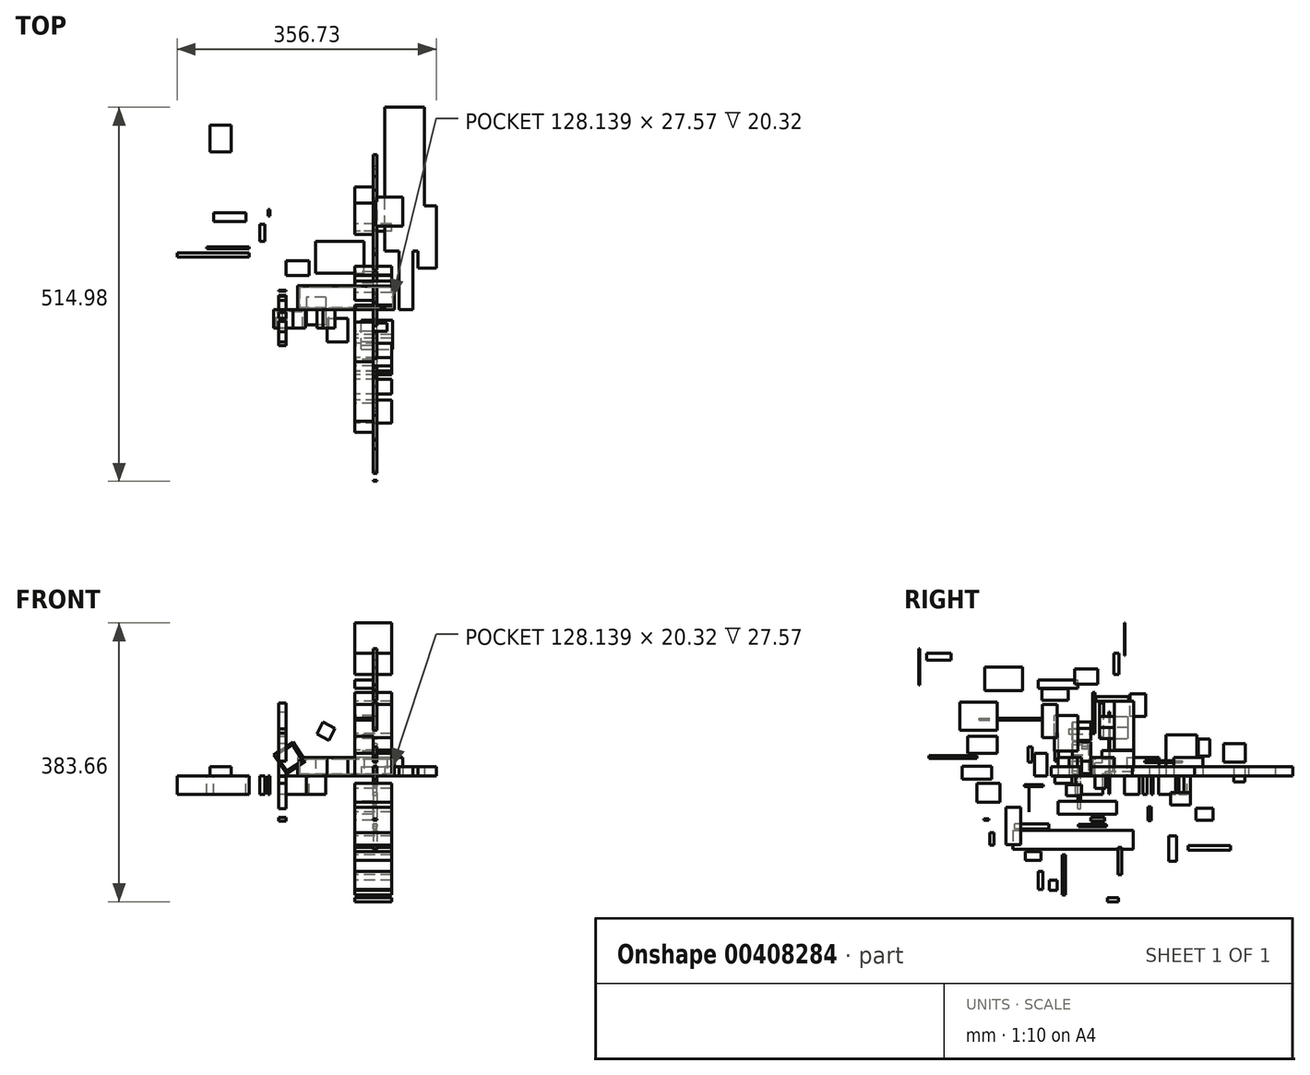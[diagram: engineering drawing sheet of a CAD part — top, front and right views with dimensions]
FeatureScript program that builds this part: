
annotation { "Feature Type Name" : "Feature", "Feature Type Description" : "" }
export const myFeature = defineFeature(function(context is Context, id is Id, definition is map)
    precondition{}
    {
        {
            var Q0;
            Q0=qCreatedBy(makeId("Top.planeOp"),FACE);
            var sketch = newSketch(context, id + "F0", { "sketchPlane" : qUnion([Q0])});
            skLineSegment(sketch, "E0.bottom", {"start": v(-38.03, -44.82) * mm, "end": v(-9.47, -44.82) * mm});
            skLineSegment(sketch, "E0.top", {"start": v(-38.03, -12.4) * mm, "end": v(-9.47, -12.4) * mm});
            skLineSegment(sketch, "E0.left", {"start": v(-38.03, -44.82) * mm, "end": v(-38.03, -12.4) * mm});
            skLineSegment(sketch, "E0.right", {"start": v(-9.47, -44.82) * mm, "end": v(-9.47, -12.4) * mm});
            skLineSegment(sketch, "E1.bottom", {"start": v(44.25, -18.44) * mm, "end": v(0, -18.44) * mm});
            skLineSegment(sketch, "E1.top", {"start": v(44.25, -29.9) * mm, "end": v(0, -29.9) * mm});
            skLineSegment(sketch, "E1.left", {"start": v(44.25, -18.44) * mm, "end": v(44.25, -29.9) * mm});
            skLineSegment(sketch, "E1.right", {"start": v(0, -18.44) * mm, "end": v(0, -29.9) * mm});
            skLineSegment(sketch, "E2.bottom", {"start": v(54.75, 32.65) * mm, "end": v(-78.47, 32.65) * mm});
            skLineSegment(sketch, "E2.top", {"start": v(54.75, 0) * mm, "end": v(-78.47, 0) * mm});
            skLineSegment(sketch, "E2.left", {"start": v(54.75, 32.65) * mm, "end": v(54.75, 0) * mm});
            skLineSegment(sketch, "E2.right", {"start": v(-78.47, 32.65) * mm, "end": v(-78.47, 0) * mm});
            skLineSegment(sketch, "E3.bottom", {"start": v(-53.9, 49.58) * mm, "end": v(12.77, 49.58) * mm});
            skLineSegment(sketch, "E3.top", {"start": v(-53.9, 93.96) * mm, "end": v(12.77, 93.96) * mm});
            skLineSegment(sketch, "E3.left", {"start": v(-53.9, 49.58) * mm, "end": v(-53.9, 93.96) * mm});
            skLineSegment(sketch, "E3.right", {"start": v(12.77, 49.58) * mm, "end": v(12.77, 93.96) * mm});
            skLineSegment(sketch, "E4.bottom", {"start": v(28.6, 114.54) * mm, "end": v(66.24, 114.54) * mm});
            skLineSegment(sketch, "E4.top", {"start": v(28.6, 154.62) * mm, "end": v(66.24, 154.62) * mm});
            skLineSegment(sketch, "E4.left", {"start": v(28.6, 114.54) * mm, "end": v(28.6, 154.62) * mm});
            skLineSegment(sketch, "E4.right", {"start": v(66.24, 114.54) * mm, "end": v(66.24, 154.62) * mm});
            skSolve(sketch);
        }
        {
            var Q0;
            Q0 = qSketchRegion(id + "F0", true);
            extrude(context, id + "F1", {"entities" : qUnion([Q0]), "depth" : 25.4 * mm});
        }
        {
            var Q0;
            Q0=qCreatedBy(makeId("Right.planeOp"),FACE);
            var sketch = newSketch(context, id + "F2", { "sketchPlane" : qUnion([Q0])});
            skLineSegment(sketch, "E5.bottom", {"start": v(-45, -52.84) * mm, "end": v(35.7, -52.84) * mm});
            skLineSegment(sketch, "E5.top", {"start": v(-45, -35) * mm, "end": v(35.7, -35) * mm});
            skLineSegment(sketch, "E5.left", {"start": v(-45, -52.84) * mm, "end": v(-45, -35) * mm});
            skLineSegment(sketch, "E5.right", {"start": v(35.7, -52.84) * mm, "end": v(35.7, -35) * mm});
            skLineSegment(sketch, "E6.bottom", {"start": v(-18, 34.28) * mm, "end": v(-49.8, 34.28) * mm});
            skLineSegment(sketch, "E6.top", {"start": v(-18, 83.43) * mm, "end": v(-49.8, 83.43) * mm});
            skLineSegment(sketch, "E6.left", {"start": v(-18, 34.28) * mm, "end": v(-18, 83.43) * mm});
            skLineSegment(sketch, "E6.right", {"start": v(-49.8, 34.28) * mm, "end": v(-49.8, 83.43) * mm});
            skLineSegment(sketch, "E7.bottom", {"start": v(12.3, 51.35) * mm, "end": v(51.6, 51.35) * mm});
            skLineSegment(sketch, "E7.top", {"start": v(12.3, 82.1) * mm, "end": v(51.6, 82.1) * mm});
            skLineSegment(sketch, "E7.left", {"start": v(12.3, 51.35) * mm, "end": v(12.3, 82.1) * mm});
            skLineSegment(sketch, "E7.right", {"start": v(51.6, 51.35) * mm, "end": v(51.6, 82.1) * mm});
            skLineSegment(sketch, "E8.bottom", {"start": v(103.49, 56.5) * mm, "end": v(146.08, 56.5) * mm});
            skLineSegment(sketch, "E8.top", {"start": v(103.49, 0) * mm, "end": v(146.08, 0) * mm});
            skLineSegment(sketch, "E8.left", {"start": v(103.49, 56.5) * mm, "end": v(103.49, 0) * mm});
            skLineSegment(sketch, "E8.right", {"start": v(146.08, 56.5) * mm, "end": v(146.08, 0) * mm});
            skLineSegment(sketch, "E9.bottom", {"start": v(-169.48, 54.43) * mm, "end": v(-128.98, 54.43) * mm});
            skLineSegment(sketch, "E9.top", {"start": v(-169.48, 31.07) * mm, "end": v(-128.98, 31.07) * mm});
            skLineSegment(sketch, "E9.left", {"start": v(-169.48, 54.43) * mm, "end": v(-169.48, 31.07) * mm});
            skLineSegment(sketch, "E9.right", {"start": v(-128.98, 54.43) * mm, "end": v(-128.98, 31.07) * mm});
            skLineSegment(sketch, "E10.bottom", {"start": v(-153.88, 77.11) * mm, "end": v(-68.7, 77.11) * mm});
            skLineSegment(sketch, "E10.top", {"start": v(-153.88, 79.37) * mm, "end": v(-68.7, 79.37) * mm});
            skLineSegment(sketch, "E10.left", {"start": v(-153.88, 77.11) * mm, "end": v(-153.88, 79.37) * mm});
            skLineSegment(sketch, "E10.right", {"start": v(-68.7, 77.11) * mm, "end": v(-68.7, 79.37) * mm});
            skLineSegment(sketch, "E11.bottom", {"start": v(-72.3, 120.66) * mm, "end": v(-17.7, 120.66) * mm});
            skLineSegment(sketch, "E11.top", {"start": v(-72.3, 131.98) * mm, "end": v(-17.7, 131.98) * mm});
            skLineSegment(sketch, "E11.left", {"start": v(-72.3, 120.66) * mm, "end": v(-72.3, 131.98) * mm});
            skLineSegment(sketch, "E11.right", {"start": v(-17.7, 120.66) * mm, "end": v(-17.7, 131.98) * mm});
            skLineSegment(sketch, "E12.bottom", {"start": v(144.88, -60.84) * mm, "end": v(168.58, -60.84) * mm});
            skLineSegment(sketch, "E12.top", {"start": v(144.88, -44.28) * mm, "end": v(168.58, -44.28) * mm});
            skLineSegment(sketch, "E12.left", {"start": v(144.88, -60.84) * mm, "end": v(144.88, -44.28) * mm});
            skLineSegment(sketch, "E12.right", {"start": v(168.58, -60.84) * mm, "end": v(168.58, -44.28) * mm});
            skSolve(sketch);
        }
        {
            var Q0;
            Q0 = qSketchRegion(id + "F2", true);
            extrude(context, id + "F3", {"entities" : qUnion([Q0]), "depth" : 25.4 * mm});
        }
        {
            var Q0;
            Q0=qCreatedBy(makeId("Front.planeOp"),FACE);
            var sketch = newSketch(context, id + "F4", { "sketchPlane" : qUnion([Q0])});
            skCircle(sketch, "E13.cCircle", {"center": v(-89.7, 25.02) * mm, "radius": 22.2 * mm, "construction": true});
            skLineSegment(sketch, "E13.0", {"start": v(-85.2, 46.75) * mm, "end": v(-67.97, 20.52) * mm});
            skLineSegment(sketch, "E13.1", {"start": v(-67.97, 20.52) * mm, "end": v(-94.21, 3.28) * mm});
            skLineSegment(sketch, "E13.2", {"start": v(-94.21, 3.28) * mm, "end": v(-111.44, 29.52) * mm});
            skLineSegment(sketch, "E13.3", {"start": v(-111.44, 29.52) * mm, "end": v(-85.2, 46.75) * mm});
            skCircle(sketch, "E14.cCircle", {"center": v(-39.66, 61.63) * mm, "radius": 13.15 * mm, "construction": true});
            skLineSegment(sketch, "E14.0", {"start": v(-43.47, 74.22) * mm, "end": v(-27.08, 65.44) * mm});
            skLineSegment(sketch, "E14.1", {"start": v(-27.08, 65.44) * mm, "end": v(-35.85, 49.05) * mm});
            skLineSegment(sketch, "E14.2", {"start": v(-35.85, 49.05) * mm, "end": v(-52.24, 57.82) * mm});
            skLineSegment(sketch, "E14.3", {"start": v(-52.24, 57.82) * mm, "end": v(-43.47, 74.22) * mm});
            skSolve(sketch);
        }
        {
            var Q0;
            Q0=makeQuery(id+"F4.imprint","IMPRINT",FACE,{"disambiguationData":[TD([[makeQuery(id+"F4.imprint","IMPRINT",EDGE,{"derivedFrom":sQuery(id+"F4.wireOp",EDGE,"E13.0")}),-1.0]])]});
            var Q1;
            Q1=makeQuery(id+"F4.imprint","IMPRINT",FACE,{"disambiguationData":[TD([[makeQuery(id+"F4.imprint","IMPRINT",EDGE,{"derivedFrom":sQuery(id+"F4.wireOp",EDGE,"E14.0")}),-1.0]])]});
            extrude(context, id + "F5", {"entities" : qUnion([Q0, Q1]), "operationType" : NewBodyOperationType.ADD, "depth" : 25.4 * mm});
        }
        {
            var Q0;
            Q0=makeQuery(id+"F5.opExtrude","CAP_FACE",FACE,{"disambiguationData":[OSD([sQuery(id+"F4.wireOp",EDGE,"E13.0"),sQuery(id+"F4.wireOp",EDGE,"E13.1"),sQuery(id+"F4.wireOp",EDGE,"E13.2"),sQuery(id+"F4.wireOp",EDGE,"E13.3")])],"isStart":false});
            shell(context, id + "F6", {"entities" : qUnion([Q0]), "thickness" : 2.54 * mm});
        }
        {
            var Q0;
            Q0=qCreatedBy(makeId("Top.planeOp"),FACE);
            var sketch = newSketch(context, id + "F7", { "sketchPlane" : qUnion([Q0])});
            skLineSegment(sketch, "E15.bottom", {"start": v(8.87, -54.8) * mm, "end": v(52.17, -54.8) * mm});
            skLineSegment(sketch, "E15.top", {"start": v(8.87, -14.7) * mm, "end": v(52.17, -14.7) * mm});
            skLineSegment(sketch, "E15.left", {"start": v(8.87, -54.8) * mm, "end": v(8.87, -14.7) * mm});
            skLineSegment(sketch, "E15.right", {"start": v(52.17, -54.8) * mm, "end": v(52.17, -14.7) * mm});
            skLineSegment(sketch, "E16.bottom", {"start": v(61.23, 0) * mm, "end": v(79.8, 0) * mm});
            skLineSegment(sketch, "E16.top", {"start": v(61.23, 87.38) * mm, "end": v(79.8, 87.38) * mm});
            skLineSegment(sketch, "E16.left", {"start": v(61.23, 0) * mm, "end": v(61.23, 87.38) * mm});
            skLineSegment(sketch, "E16.right", {"start": v(79.8, 0) * mm, "end": v(79.8, 87.38) * mm});
            skLineSegment(sketch, "E17.bottom", {"start": v(-170.1, 253.84) * mm, "end": v(-199.66, 253.84) * mm});
            skLineSegment(sketch, "E17.top", {"start": v(-170.1, 217.1) * mm, "end": v(-199.66, 217.1) * mm});
            skLineSegment(sketch, "E17.left", {"start": v(-170.1, 253.84) * mm, "end": v(-170.1, 217.1) * mm});
            skLineSegment(sketch, "E17.right", {"start": v(-199.66, 253.84) * mm, "end": v(-199.66, 217.1) * mm});
            skLineSegment(sketch, "E18.bottom", {"start": v(96.2, 80.64) * mm, "end": v(41.3, 80.64) * mm});
            skLineSegment(sketch, "E18.top", {"start": v(96.2, 278.22) * mm, "end": v(41.3, 278.22) * mm});
            skLineSegment(sketch, "E18.left", {"start": v(96.2, 80.64) * mm, "end": v(96.2, 278.22) * mm});
            skLineSegment(sketch, "E18.right", {"start": v(41.3, 80.64) * mm, "end": v(41.3, 278.22) * mm});
            skLineSegment(sketch, "E19.bottom", {"start": v(112.24, 57.15) * mm, "end": v(87.1, 57.15) * mm});
            skLineSegment(sketch, "E19.top", {"start": v(112.24, 142.89) * mm, "end": v(87.1, 142.89) * mm});
            skLineSegment(sketch, "E19.left", {"start": v(112.24, 57.15) * mm, "end": v(112.24, 142.89) * mm});
            skLineSegment(sketch, "E19.right", {"start": v(87.1, 57.15) * mm, "end": v(87.1, 142.89) * mm});
            skSolve(sketch);
        }
        {
            var Q0;
            Q0 = qSketchRegion(id + "F7", true);
            extrude(context, id + "F8", {"entities" : qUnion([Q0]), "depth" : 12.7 * mm});
        }
        {
            var Q0;
            Q0=makeQuery(id+"F3.opExtrude","CAP_FACE",FACE,{"disambiguationData":[OSD([sQuery(id+"F2.wireOp",EDGE,"E7.bottom"),sQuery(id+"F2.wireOp",EDGE,"E7.top"),sQuery(id+"F2.wireOp",EDGE,"E7.left"),sQuery(id+"F2.wireOp",EDGE,"E7.right")])],"isStart":false});
            var sketch = newSketch(context, id + "F9", { "sketchPlane" : qUnion([Q0])});
            skLineSegment(sketch, "E20.bottom", {"start": v(-22.37, 126.65) * mm, "end": v(9.5, 126.65) * mm});
            skLineSegment(sketch, "E20.top", {"start": v(-22.37, 147.22) * mm, "end": v(9.5, 147.22) * mm});
            skLineSegment(sketch, "E20.left", {"start": v(-22.37, 126.65) * mm, "end": v(-22.37, 147.22) * mm});
            skLineSegment(sketch, "E20.right", {"start": v(9.5, 126.65) * mm, "end": v(9.5, 147.22) * mm});
            skPoint(sketch, "E21.firstSnap0", {"position": v(12.3, 66.72) * mm});
            skPoint(sketch, "E21.oppositeSnap0", {"position": v(12.3, 66.72) * mm});
            skLineSegment(sketch, "E21.bottom", {"start": v(39.3, 66.72) * mm, "end": v(63.45, 66.72) * mm});
            skLineSegment(sketch, "E21.top", {"start": v(39.3, 66.72) * mm, "end": v(63.45, 66.72) * mm});
            skLineSegment(sketch, "E21.left", {"start": v(39.3, 66.72) * mm, "end": v(39.3, 66.72) * mm});
            skLineSegment(sketch, "E21.right", {"start": v(63.45, 66.72) * mm, "end": v(63.45, 66.72) * mm});
            skLineSegment(sketch, "E22.bottom", {"start": v(51.38, 66.72) * mm, "end": v(12.3, 66.72) * mm});
            skLineSegment(sketch, "E22.top", {"start": v(51.38, 82.1) * mm, "end": v(12.3, 82.1) * mm});
            skLineSegment(sketch, "E22.left", {"start": v(51.38, 66.72) * mm, "end": v(51.38, 82.1) * mm});
            skLineSegment(sketch, "E22.right", {"start": v(12.3, 66.72) * mm, "end": v(12.3, 82.1) * mm});
            skLineSegment(sketch, "E23.bottom", {"start": v(75.5, 81.79) * mm, "end": v(54.2, 81.79) * mm});
            skLineSegment(sketch, "E23.top", {"start": v(75.5, 113.11) * mm, "end": v(54.2, 113.11) * mm});
            skLineSegment(sketch, "E23.left", {"start": v(75.5, 81.79) * mm, "end": v(75.5, 113.11) * mm});
            skLineSegment(sketch, "E23.right", {"start": v(54.2, 81.79) * mm, "end": v(54.2, 113.11) * mm});
            skLineSegment(sketch, "E24.bottom", {"start": v(52.46, 109.2) * mm, "end": v(6.87, 109.2) * mm});
            skLineSegment(sketch, "E24.top", {"start": v(52.46, 103.02) * mm, "end": v(6.87, 103.02) * mm});
            skLineSegment(sketch, "E24.left", {"start": v(52.46, 109.2) * mm, "end": v(52.46, 103.02) * mm});
            skLineSegment(sketch, "E24.right", {"start": v(6.87, 109.2) * mm, "end": v(6.87, 103.02) * mm});
            skLineSegment(sketch, "E25.bottom", {"start": v(-31, 104.25) * mm, "end": v(-67.36, 104.25) * mm});
            skLineSegment(sketch, "E25.top", {"start": v(-31, 120.08) * mm, "end": v(-67.36, 120.08) * mm});
            skLineSegment(sketch, "E25.left", {"start": v(-31, 104.25) * mm, "end": v(-31, 120.08) * mm});
            skLineSegment(sketch, "E25.right", {"start": v(-67.36, 104.25) * mm, "end": v(-67.36, 120.08) * mm});
            skLineSegment(sketch, "E26.bottom", {"start": v(-93.6, 117.55) * mm, "end": v(-145.86, 117.55) * mm});
            skLineSegment(sketch, "E26.top", {"start": v(-93.6, 149.62) * mm, "end": v(-145.86, 149.62) * mm});
            skLineSegment(sketch, "E26.left", {"start": v(-93.6, 117.55) * mm, "end": v(-93.6, 149.62) * mm});
            skLineSegment(sketch, "E26.right", {"start": v(-145.86, 117.55) * mm, "end": v(-145.86, 149.62) * mm});
            skLineSegment(sketch, "E27.bottom", {"start": v(-192.33, 159.6) * mm, "end": v(-225.98, 159.6) * mm});
            skLineSegment(sketch, "E27.top", {"start": v(-192.33, 169.05) * mm, "end": v(-225.98, 169.05) * mm});
            skLineSegment(sketch, "E27.left", {"start": v(-192.33, 159.6) * mm, "end": v(-192.33, 169.05) * mm});
            skLineSegment(sketch, "E27.right", {"start": v(-225.98, 159.6) * mm, "end": v(-225.98, 169.05) * mm});
            skLineSegment(sketch, "E28.bottom", {"start": v(-236.76, 175.63) * mm, "end": v(-235.24, 175.63) * mm});
            skLineSegment(sketch, "E28.top", {"start": v(-236.76, 125.14) * mm, "end": v(-235.24, 125.14) * mm});
            skLineSegment(sketch, "E28.left", {"start": v(-236.76, 175.63) * mm, "end": v(-236.76, 125.14) * mm});
            skLineSegment(sketch, "E28.right", {"start": v(-235.24, 175.63) * mm, "end": v(-235.24, 125.14) * mm});
            skLineSegment(sketch, "E29.bottom", {"start": v(-180.07, 101.93) * mm, "end": v(-128.76, 101.93) * mm});
            skLineSegment(sketch, "E29.top", {"start": v(-180.07, 62.9) * mm, "end": v(-128.76, 62.9) * mm});
            skLineSegment(sketch, "E29.left", {"start": v(-180.07, 101.93) * mm, "end": v(-180.07, 62.9) * mm});
            skLineSegment(sketch, "E29.right", {"start": v(-128.76, 101.93) * mm, "end": v(-128.76, 62.9) * mm});
            skLineSegment(sketch, "E30.bottom", {"start": v(-86.12, 40.02) * mm, "end": v(-80.28, 40.02) * mm});
            skLineSegment(sketch, "E30.top", {"start": v(-86.12, 19.17) * mm, "end": v(-80.28, 19.17) * mm});
            skLineSegment(sketch, "E30.left", {"start": v(-86.12, 40.02) * mm, "end": v(-86.12, 19.17) * mm});
            skLineSegment(sketch, "E30.right", {"start": v(-80.28, 40.02) * mm, "end": v(-80.28, 19.17) * mm});
            skLineSegment(sketch, "E31.bottom", {"start": v(-156.85, 24.07) * mm, "end": v(-222.57, 24.07) * mm});
            skLineSegment(sketch, "E31.top", {"start": v(-156.85, 28.24) * mm, "end": v(-222.57, 28.24) * mm});
            skLineSegment(sketch, "E31.left", {"start": v(-156.85, 24.07) * mm, "end": v(-156.85, 28.24) * mm});
            skLineSegment(sketch, "E31.right", {"start": v(-222.57, 24.07) * mm, "end": v(-222.57, 28.24) * mm});
            skLineSegment(sketch, "E32.bottom", {"start": v(-177.26, 13.33) * mm, "end": v(-136.14, 13.33) * mm});
            skLineSegment(sketch, "E32.top", {"start": v(-177.26, -4.55) * mm, "end": v(-136.14, -4.55) * mm});
            skLineSegment(sketch, "E32.left", {"start": v(-177.26, 13.33) * mm, "end": v(-177.26, -4.55) * mm});
            skLineSegment(sketch, "E32.right", {"start": v(-136.14, 13.33) * mm, "end": v(-136.14, -4.55) * mm});
            skLineSegment(sketch, "E33.bottom", {"start": v(-91.53, -12.28) * mm, "end": v(-65.22, -12.28) * mm});
            skLineSegment(sketch, "E33.top", {"start": v(-91.53, -14.84) * mm, "end": v(-65.22, -14.84) * mm});
            skLineSegment(sketch, "E33.left", {"start": v(-91.53, -12.28) * mm, "end": v(-91.53, -14.84) * mm});
            skLineSegment(sketch, "E33.right", {"start": v(-65.22, -12.28) * mm, "end": v(-65.22, -14.84) * mm});
            skLineSegment(sketch, "E34.bottom", {"start": v(-33.36, -27.12) * mm, "end": v(-12.85, -27.12) * mm});
            skLineSegment(sketch, "E34.top", {"start": v(-33.36, -12.23) * mm, "end": v(-12.85, -12.23) * mm});
            skLineSegment(sketch, "E34.left", {"start": v(-33.36, -27.12) * mm, "end": v(-33.36, -12.23) * mm});
            skLineSegment(sketch, "E34.right", {"start": v(-12.85, -27.12) * mm, "end": v(-12.85, -12.23) * mm});
            skLineSegment(sketch, "E35.bottom", {"start": v(20.29, -17.13) * mm, "end": v(5.9, -17.13) * mm});
            skLineSegment(sketch, "E35.top", {"start": v(20.29, 17.72) * mm, "end": v(5.9, 17.72) * mm});
            skLineSegment(sketch, "E35.left", {"start": v(20.29, -17.13) * mm, "end": v(20.29, 17.72) * mm});
            skLineSegment(sketch, "E35.right", {"start": v(5.9, -17.13) * mm, "end": v(5.9, 17.72) * mm});
            skLineSegment(sketch, "E36.bottom", {"start": v(15.53, 35.04) * mm, "end": v(59.45, 35.04) * mm});
            skLineSegment(sketch, "E36.top", {"start": v(15.53, 6.29) * mm, "end": v(59.45, 6.29) * mm});
            skLineSegment(sketch, "E36.left", {"start": v(15.53, 35.04) * mm, "end": v(15.53, 6.29) * mm});
            skLineSegment(sketch, "E36.right", {"start": v(59.45, 35.04) * mm, "end": v(59.45, 6.29) * mm});
            skLineSegment(sketch, "E37.bottom", {"start": v(74.66, 20.84) * mm, "end": v(126.05, 20.84) * mm});
            skLineSegment(sketch, "E37.top", {"start": v(74.66, 18.19) * mm, "end": v(126.05, 18.19) * mm});
            skLineSegment(sketch, "E37.left", {"start": v(74.66, 20.84) * mm, "end": v(74.66, 18.19) * mm});
            skLineSegment(sketch, "E37.right", {"start": v(126.05, 20.84) * mm, "end": v(126.05, 18.19) * mm});
            skLineSegment(sketch, "E38.bottom", {"start": v(164.01, 27.43) * mm, "end": v(148.04, 27.43) * mm});
            skLineSegment(sketch, "E38.top", {"start": v(164.01, 51.07) * mm, "end": v(148.04, 51.07) * mm});
            skLineSegment(sketch, "E38.left", {"start": v(164.01, 27.43) * mm, "end": v(164.01, 51.07) * mm});
            skLineSegment(sketch, "E38.right", {"start": v(148.04, 27.43) * mm, "end": v(148.04, 51.07) * mm});
            skLineSegment(sketch, "E39.bottom", {"start": v(182.96, 44.39) * mm, "end": v(212.85, 44.39) * mm});
            skLineSegment(sketch, "E39.top", {"start": v(182.96, 19.27) * mm, "end": v(212.85, 19.27) * mm});
            skLineSegment(sketch, "E39.left", {"start": v(182.96, 44.39) * mm, "end": v(182.96, 19.27) * mm});
            skLineSegment(sketch, "E39.right", {"start": v(212.85, 44.39) * mm, "end": v(212.85, 19.27) * mm});
            skLineSegment(sketch, "E40.bottom", {"start": v(212.17, 11.5) * mm, "end": v(197.14, 11.5) * mm});
            skLineSegment(sketch, "E40.top", {"start": v(212.17, -8) * mm, "end": v(197.14, -8) * mm});
            skLineSegment(sketch, "E40.left", {"start": v(212.17, 11.5) * mm, "end": v(212.17, -8) * mm});
            skLineSegment(sketch, "E40.right", {"start": v(197.14, 11.5) * mm, "end": v(197.14, -8) * mm});
            skLineSegment(sketch, "E41.bottom", {"start": v(137.05, -22.66) * mm, "end": v(110.1, -22.66) * mm});
            skLineSegment(sketch, "E41.top", {"start": v(137.05, -39.9) * mm, "end": v(110.1, -39.9) * mm});
            skLineSegment(sketch, "E41.left", {"start": v(137.05, -22.66) * mm, "end": v(137.05, -39.9) * mm});
            skLineSegment(sketch, "E41.right", {"start": v(110.1, -22.66) * mm, "end": v(110.1, -39.9) * mm});
            skLineSegment(sketch, "E42.bottom", {"start": v(83.23, -42.66) * mm, "end": v(78.69, -42.66) * mm});
            skLineSegment(sketch, "E42.top", {"start": v(83.23, -61.61) * mm, "end": v(78.69, -61.61) * mm});
            skLineSegment(sketch, "E42.left", {"start": v(83.23, -42.66) * mm, "end": v(83.23, -61.61) * mm});
            skLineSegment(sketch, "E42.right", {"start": v(78.69, -42.66) * mm, "end": v(78.69, -61.61) * mm});
            skLineSegment(sketch, "E43.bottom", {"start": v(21.45, -66.33) * mm, "end": v(-17.18, -66.33) * mm});
            skLineSegment(sketch, "E43.top", {"start": v(21.45, -70.08) * mm, "end": v(-17.18, -70.08) * mm});
            skLineSegment(sketch, "E43.left", {"start": v(21.45, -66.33) * mm, "end": v(21.45, -70.08) * mm});
            skLineSegment(sketch, "E43.right", {"start": v(-17.18, -66.33) * mm, "end": v(-17.18, -70.08) * mm});
            skLineSegment(sketch, "E44.bottom", {"start": v(-57.95, -73.06) * mm, "end": v(-104.88, -73.06) * mm});
            skLineSegment(sketch, "E44.top", {"start": v(-57.95, -65.95) * mm, "end": v(-104.88, -65.95) * mm});
            skLineSegment(sketch, "E44.left", {"start": v(-57.95, -73.06) * mm, "end": v(-57.95, -65.95) * mm});
            skLineSegment(sketch, "E44.right", {"start": v(-104.88, -73.06) * mm, "end": v(-104.88, -65.95) * mm});
            skLineSegment(sketch, "E45.bottom", {"start": v(-140.49, -60.7) * mm, "end": v(-146.94, -60.7) * mm});
            skLineSegment(sketch, "E45.top", {"start": v(-140.49, -59.04) * mm, "end": v(-146.94, -59.04) * mm});
            skLineSegment(sketch, "E45.left", {"start": v(-140.49, -60.7) * mm, "end": v(-140.49, -59.04) * mm});
            skLineSegment(sketch, "E45.right", {"start": v(-146.94, -60.7) * mm, "end": v(-146.94, -59.04) * mm});
            skLineSegment(sketch, "E46.bottom", {"start": v(-107.38, -74.85) * mm, "end": v(58.57, -74.85) * mm});
            skLineSegment(sketch, "E46.top", {"start": v(-107.38, -100.77) * mm, "end": v(58.57, -100.77) * mm});
            skLineSegment(sketch, "E46.left", {"start": v(-107.38, -74.85) * mm, "end": v(-107.38, -100.77) * mm});
            skLineSegment(sketch, "E46.right", {"start": v(58.57, -74.85) * mm, "end": v(58.57, -100.77) * mm});
            skLineSegment(sketch, "E47.bottom", {"start": v(134.37, -95.7) * mm, "end": v(192.62, -95.7) * mm});
            skLineSegment(sketch, "E47.top", {"start": v(134.37, -102.38) * mm, "end": v(192.62, -102.38) * mm});
            skLineSegment(sketch, "E47.left", {"start": v(134.37, -95.7) * mm, "end": v(134.37, -102.38) * mm});
            skLineSegment(sketch, "E47.right", {"start": v(192.62, -95.7) * mm, "end": v(192.62, -102.38) * mm});
            skSolve(sketch);
        }
        {
            var Q0;
            Q0 = qSketchRegion(id + "F9", true);
            extrude(context, id + "F10", {"entities" : qUnion([Q0]), "depth" : 5.08 * mm});
        }
        {
            var Q0;
            Q0=makeQuery(id+"F1.opExtrude","CAP_FACE",FACE,{"disambiguationData":[OSD([sQuery(id+"F0.wireOp",EDGE,"E3.bottom"),sQuery(id+"F0.wireOp",EDGE,"E3.top"),sQuery(id+"F0.wireOp",EDGE,"E3.left"),sQuery(id+"F0.wireOp",EDGE,"E3.right")])],"isStart":true});
            var sketch = newSketch(context, id + "F11", { "sketchPlane" : qUnion([Q0])});
            skLineSegment(sketch, "E48.bottom", {"start": v(-145.44, -71.9) * mm, "end": v(-244.49, -71.9) * mm});
            skLineSegment(sketch, "E48.top", {"start": v(-145.44, -77.69) * mm, "end": v(-244.49, -77.69) * mm});
            skLineSegment(sketch, "E48.left", {"start": v(-145.44, -71.9) * mm, "end": v(-145.44, -77.69) * mm});
            skLineSegment(sketch, "E48.right", {"start": v(-244.49, -71.9) * mm, "end": v(-244.49, -77.69) * mm});
            skLineSegment(sketch, "E49.bottom", {"start": v(-203.97, -83.42) * mm, "end": v(-145.4, -83.42) * mm});
            skLineSegment(sketch, "E49.top", {"start": v(-203.97, -86.1) * mm, "end": v(-145.4, -86.1) * mm});
            skLineSegment(sketch, "E49.left", {"start": v(-203.97, -83.42) * mm, "end": v(-203.97, -86.1) * mm});
            skLineSegment(sketch, "E49.right", {"start": v(-145.4, -83.42) * mm, "end": v(-145.4, -86.1) * mm});
            skLineSegment(sketch, "E50.bottom", {"start": v(-123.86, -93.54) * mm, "end": v(-130.72, -93.54) * mm});
            skLineSegment(sketch, "E50.top", {"start": v(-123.86, -117.2) * mm, "end": v(-130.72, -117.2) * mm});
            skLineSegment(sketch, "E50.left", {"start": v(-123.86, -93.54) * mm, "end": v(-123.86, -117.2) * mm});
            skLineSegment(sketch, "E50.right", {"start": v(-130.72, -93.54) * mm, "end": v(-130.72, -117.2) * mm});
            skLineSegment(sketch, "E51.bottom", {"start": v(-194.53, -121.18) * mm, "end": v(-149.9, -121.18) * mm});
            skLineSegment(sketch, "E51.top", {"start": v(-194.53, -132.9) * mm, "end": v(-149.9, -132.9) * mm});
            skLineSegment(sketch, "E51.left", {"start": v(-194.53, -121.18) * mm, "end": v(-194.53, -132.9) * mm});
            skLineSegment(sketch, "E51.right", {"start": v(-149.9, -121.18) * mm, "end": v(-149.9, -132.9) * mm});
            skLineSegment(sketch, "E52.bottom", {"start": v(-119.65, -137.4) * mm, "end": v(-116.93, -137.4) * mm});
            skLineSegment(sketch, "E52.top", {"start": v(-119.65, -128.39) * mm, "end": v(-116.93, -128.39) * mm});
            skLineSegment(sketch, "E52.left", {"start": v(-119.65, -137.4) * mm, "end": v(-119.65, -128.39) * mm});
            skLineSegment(sketch, "E52.right", {"start": v(-116.93, -137.4) * mm, "end": v(-116.93, -128.39) * mm});
            skLineSegment(sketch, "E53.bottom", {"start": v(-94.3, -66.77) * mm, "end": v(-63.06, -66.77) * mm});
            skLineSegment(sketch, "E53.top", {"start": v(-94.3, -46.68) * mm, "end": v(-63.06, -46.68) * mm});
            skLineSegment(sketch, "E53.left", {"start": v(-94.3, -66.77) * mm, "end": v(-94.3, -46.68) * mm});
            skLineSegment(sketch, "E53.right", {"start": v(-63.06, -66.77) * mm, "end": v(-63.06, -46.68) * mm});
            skLineSegment(sketch, "E54.bottom", {"start": v(-40, -16.7) * mm, "end": v(-66.45, -16.7) * mm});
            skLineSegment(sketch, "E54.top", {"start": v(-40, 21) * mm, "end": v(-66.45, 21) * mm});
            skLineSegment(sketch, "E54.left", {"start": v(-40, -16.7) * mm, "end": v(-40, 21) * mm});
            skLineSegment(sketch, "E54.right", {"start": v(-66.45, -16.7) * mm, "end": v(-66.45, 21) * mm});
            skSolve(sketch);
        }
        {
            var Q0;
            Q0 = qSketchRegion(id + "F11", true);
            extrude(context, id + "F12", {"entities" : qUnion([Q0]), "operationType" : NewBodyOperationType.ADD, "depth" : 25.4 * mm});
        }
        {
            var Q0;
            Q0=makeQuery(id+"F12.opExtrude","SWEPT_FACE",FACE,{"disambiguationData":[OSD([sQuery(id+"F11.wireOp",EDGE,"E53.left")])]});
            var sketch = newSketch(context, id + "F13", { "sketchPlane" : qUnion([Q0])});
            skLineSegment(sketch, "E55.bottom", {"start": v(-19.4, -56.89) * mm, "end": v(0, -56.89) * mm});
            skLineSegment(sketch, "E55.top", {"start": v(-19.4, -61.93) * mm, "end": v(0, -61.93) * mm});
            skLineSegment(sketch, "E55.left", {"start": v(-19.4, -56.89) * mm, "end": v(-19.4, -61.93) * mm});
            skLineSegment(sketch, "E55.right", {"start": v(0, -56.89) * mm, "end": v(0, -61.93) * mm});
            skLineSegment(sketch, "E56.bottom", {"start": v(17.42, -45.07) * mm, "end": v(13.8, -45.07) * mm});
            skLineSegment(sketch, "E56.top", {"start": v(17.42, 0) * mm, "end": v(13.8, 0) * mm});
            skLineSegment(sketch, "E56.left", {"start": v(17.42, -45.07) * mm, "end": v(17.42, 0) * mm});
            skLineSegment(sketch, "E56.right", {"start": v(13.8, -45.07) * mm, "end": v(13.8, 0) * mm});
            skLineSegment(sketch, "E57.bottom", {"start": v(26, -10.05) * mm, "end": v(49.7, -10.05) * mm});
            skLineSegment(sketch, "E57.top", {"start": v(26, -0.43) * mm, "end": v(49.7, -0.43) * mm});
            skLineSegment(sketch, "E57.left", {"start": v(26, -10.05) * mm, "end": v(26, -0.43) * mm});
            skLineSegment(sketch, "E57.right", {"start": v(49.7, -10.05) * mm, "end": v(49.7, -0.43) * mm});
            skLineSegment(sketch, "E58.bottom", {"start": v(49.53, 20.68) * mm, "end": v(44.43, 20.68) * mm});
            skLineSegment(sketch, "E58.top", {"start": v(49.53, 59.35) * mm, "end": v(44.43, 59.35) * mm});
            skLineSegment(sketch, "E58.left", {"start": v(49.53, 20.68) * mm, "end": v(49.53, 59.35) * mm});
            skLineSegment(sketch, "E58.right", {"start": v(44.43, 20.68) * mm, "end": v(44.43, 59.35) * mm});
            skLineSegment(sketch, "E59.bottom", {"start": v(30.6, 64.54) * mm, "end": v(16.19, 64.54) * mm});
            skLineSegment(sketch, "E59.top", {"start": v(30.6, 58.13) * mm, "end": v(16.19, 58.13) * mm});
            skLineSegment(sketch, "E59.left", {"start": v(30.6, 64.54) * mm, "end": v(30.6, 58.13) * mm});
            skLineSegment(sketch, "E59.right", {"start": v(16.19, 64.54) * mm, "end": v(16.19, 58.13) * mm});
            skLineSegment(sketch, "E60.bottom", {"start": v(12.15, 45.41) * mm, "end": v(4.2, 45.41) * mm});
            skLineSegment(sketch, "E60.top", {"start": v(12.15, 36.91) * mm, "end": v(4.2, 36.91) * mm});
            skLineSegment(sketch, "E60.left", {"start": v(12.15, 45.41) * mm, "end": v(12.15, 36.91) * mm});
            skLineSegment(sketch, "E60.right", {"start": v(4.2, 45.41) * mm, "end": v(4.2, 36.91) * mm});
            skLineSegment(sketch, "E61.bottom", {"start": v(-12.35, 54.8) * mm, "end": v(-17.92, 54.8) * mm});
            skLineSegment(sketch, "E61.top", {"start": v(-12.35, 100.6) * mm, "end": v(-17.92, 100.6) * mm});
            skLineSegment(sketch, "E61.left", {"start": v(-12.35, 54.8) * mm, "end": v(-12.35, 100.6) * mm});
            skLineSegment(sketch, "E61.right", {"start": v(-17.92, 54.8) * mm, "end": v(-17.92, 100.6) * mm});
            skLineSegment(sketch, "E62.bottom", {"start": v(-25.12, 88.16) * mm, "end": v(-26.09, 88.16) * mm});
            skLineSegment(sketch, "E62.top", {"start": v(-25.12, -24.55) * mm, "end": v(-26.09, -24.55) * mm});
            skLineSegment(sketch, "E62.left", {"start": v(-25.12, 88.16) * mm, "end": v(-25.12, -24.55) * mm});
            skLineSegment(sketch, "E62.right", {"start": v(-26.09, 88.16) * mm, "end": v(-26.09, -24.55) * mm});
            skSolve(sketch);
        }
        {
            var Q0;
            Q0 = qSketchRegion(id + "F13", true);
            extrude(context, id + "F14", {"entities" : qUnion([Q0]), "operationType" : NewBodyOperationType.ADD, "depth" : 10.16 * mm});
        }
        {
            var Q0;
            Q0=qCreatedBy(makeId("Right.planeOp"),FACE);
            var sketch = newSketch(context, id + "F15", { "sketchPlane" : qUnion([Q0])});
            skLineSegment(sketch, "E63.bottom", {"start": v(-46.45, 98.2) * mm, "end": v(-66.44, 98.2) * mm});
            skLineSegment(sketch, "E63.top", {"start": v(-46.45, 52.59) * mm, "end": v(-66.44, 52.59) * mm});
            skLineSegment(sketch, "E63.left", {"start": v(-46.45, 98.2) * mm, "end": v(-46.45, 52.59) * mm});
            skLineSegment(sketch, "E63.right", {"start": v(-66.44, 98.2) * mm, "end": v(-66.44, 52.59) * mm});
            skLineSegment(sketch, "E64.bottom", {"start": v(-77.65, 0) * mm, "end": v(-60.5, 0) * mm});
            skLineSegment(sketch, "E64.top", {"start": v(-77.65, 31.05) * mm, "end": v(-60.5, 31.05) * mm});
            skLineSegment(sketch, "E64.left", {"start": v(-77.65, 0) * mm, "end": v(-77.65, 31.05) * mm});
            skLineSegment(sketch, "E64.right", {"start": v(-60.5, 0) * mm, "end": v(-60.5, 31.05) * mm});
            skLineSegment(sketch, "E65.bottom", {"start": v(-84.92, -17.35) * mm, "end": v(-85.1, -17.35) * mm});
            skLineSegment(sketch, "E65.top", {"start": v(-84.92, -49.14) * mm, "end": v(-85.1, -49.14) * mm});
            skLineSegment(sketch, "E65.left", {"start": v(-84.92, -17.35) * mm, "end": v(-84.92, -49.14) * mm});
            skLineSegment(sketch, "E65.right", {"start": v(-85.1, -17.35) * mm, "end": v(-85.1, -49.14) * mm});
            skLineSegment(sketch, "E66.bottom", {"start": v(-96.41, -42.8) * mm, "end": v(-116.68, -42.8) * mm});
            skLineSegment(sketch, "E66.top", {"start": v(-96.41, -94.67) * mm, "end": v(-116.68, -94.67) * mm});
            skLineSegment(sketch, "E66.left", {"start": v(-96.41, -42.8) * mm, "end": v(-96.41, -94.67) * mm});
            skLineSegment(sketch, "E66.right", {"start": v(-116.68, -42.8) * mm, "end": v(-116.68, -94.67) * mm});
            skLineSegment(sketch, "E67.bottom", {"start": v(32.55, 35.91) * mm, "end": v(59.19, 35.91) * mm});
            skLineSegment(sketch, "E67.top", {"start": v(32.55, 102.91) * mm, "end": v(59.19, 102.91) * mm});
            skLineSegment(sketch, "E67.left", {"start": v(32.55, 35.91) * mm, "end": v(32.55, 102.91) * mm});
            skLineSegment(sketch, "E67.right", {"start": v(59.19, 35.91) * mm, "end": v(59.19, 102.91) * mm});
            skLineSegment(sketch, "E68.bottom", {"start": v(47.2, 165.63) * mm, "end": v(46.67, 165.63) * mm});
            skLineSegment(sketch, "E68.top", {"start": v(47.2, 210.6) * mm, "end": v(46.67, 210.6) * mm});
            skLineSegment(sketch, "E68.left", {"start": v(47.2, 165.63) * mm, "end": v(47.2, 210.6) * mm});
            skLineSegment(sketch, "E68.right", {"start": v(46.67, 165.63) * mm, "end": v(46.67, 210.6) * mm});
            skLineSegment(sketch, "E69.bottom", {"start": v(38.93, 169.27) * mm, "end": v(31.84, 169.27) * mm});
            skLineSegment(sketch, "E69.top", {"start": v(38.93, 139.76) * mm, "end": v(31.84, 139.76) * mm});
            skLineSegment(sketch, "E69.left", {"start": v(38.93, 169.27) * mm, "end": v(38.93, 139.76) * mm});
            skLineSegment(sketch, "E69.right", {"start": v(31.84, 169.27) * mm, "end": v(31.84, 139.76) * mm});
            skLineSegment(sketch, "E70.bottom", {"start": v(2.4, 114.9) * mm, "end": v(5.77, 114.9) * mm});
            skLineSegment(sketch, "E70.top", {"start": v(2.4, 58.5) * mm, "end": v(5.77, 58.5) * mm});
            skLineSegment(sketch, "E70.left", {"start": v(2.4, 114.9) * mm, "end": v(2.4, 58.5) * mm});
            skLineSegment(sketch, "E70.right", {"start": v(5.77, 114.9) * mm, "end": v(5.77, 58.5) * mm});
            skLineSegment(sketch, "E71.bottom", {"start": v(-34.88, -108.45) * mm, "end": v(-39.35, -108.45) * mm});
            skLineSegment(sketch, "E71.top", {"start": v(-34.88, -164.03) * mm, "end": v(-39.35, -164.03) * mm});
            skLineSegment(sketch, "E71.left", {"start": v(-34.88, -108.45) * mm, "end": v(-34.88, -164.03) * mm});
            skLineSegment(sketch, "E71.right", {"start": v(-39.35, -108.45) * mm, "end": v(-39.35, -164.03) * mm});
            skLineSegment(sketch, "E72.bottom", {"start": v(-57.2, -143.43) * mm, "end": v(-46.52, -143.43) * mm});
            skLineSegment(sketch, "E72.top", {"start": v(-57.2, -157.45) * mm, "end": v(-46.52, -157.45) * mm});
            skLineSegment(sketch, "E72.left", {"start": v(-57.2, -143.43) * mm, "end": v(-57.2, -157.45) * mm});
            skLineSegment(sketch, "E72.right", {"start": v(-46.52, -143.43) * mm, "end": v(-46.52, -157.45) * mm});
            skLineSegment(sketch, "E73.bottom", {"start": v(-72.47, -131.33) * mm, "end": v(-65.8, -131.33) * mm});
            skLineSegment(sketch, "E73.top", {"start": v(-72.47, -156.45) * mm, "end": v(-65.8, -156.45) * mm});
            skLineSegment(sketch, "E73.left", {"start": v(-72.47, -131.33) * mm, "end": v(-72.47, -156.45) * mm});
            skLineSegment(sketch, "E73.right", {"start": v(-65.8, -131.33) * mm, "end": v(-65.8, -156.45) * mm});
            skLineSegment(sketch, "E74.bottom", {"start": v(-90.07, -116.4) * mm, "end": v(-68.19, -116.4) * mm});
            skLineSegment(sketch, "E74.top", {"start": v(-90.07, -103.83) * mm, "end": v(-68.19, -103.83) * mm});
            skLineSegment(sketch, "E74.left", {"start": v(-90.07, -116.4) * mm, "end": v(-90.07, -103.83) * mm});
            skLineSegment(sketch, "E74.right", {"start": v(-68.19, -116.4) * mm, "end": v(-68.19, -103.83) * mm});
            skLineSegment(sketch, "E75.bottom", {"start": v(22.96, -167.56) * mm, "end": v(38.16, -167.56) * mm});
            skLineSegment(sketch, "E75.top", {"start": v(22.96, -173.07) * mm, "end": v(38.16, -173.07) * mm});
            skLineSegment(sketch, "E75.left", {"start": v(22.96, -167.56) * mm, "end": v(22.96, -173.07) * mm});
            skLineSegment(sketch, "E75.right", {"start": v(38.16, -167.56) * mm, "end": v(38.16, -173.07) * mm});
            skLineSegment(sketch, "E76.bottom", {"start": v(37.57, -135.77) * mm, "end": v(42.6, -135.77) * mm});
            skLineSegment(sketch, "E76.top", {"start": v(37.57, -98.55) * mm, "end": v(42.6, -98.55) * mm});
            skLineSegment(sketch, "E76.left", {"start": v(37.57, -135.77) * mm, "end": v(37.57, -98.55) * mm});
            skLineSegment(sketch, "E76.right", {"start": v(42.6, -135.77) * mm, "end": v(42.6, -98.55) * mm});
            skLineSegment(sketch, "E77.bottom", {"start": v(107.48, -82.46) * mm, "end": v(118.01, -82.46) * mm});
            skLineSegment(sketch, "E77.top", {"start": v(107.48, -117.3) * mm, "end": v(118.01, -117.3) * mm});
            skLineSegment(sketch, "E77.left", {"start": v(107.48, -82.46) * mm, "end": v(107.48, -117.3) * mm});
            skLineSegment(sketch, "E77.right", {"start": v(118.01, -82.46) * mm, "end": v(118.01, -117.3) * mm});
            skLineSegment(sketch, "E78.bottom", {"start": v(-124.8, -36.2) * mm, "end": v(-156.46, -36.2) * mm});
            skLineSegment(sketch, "E78.top", {"start": v(-124.8, -9.9) * mm, "end": v(-156.46, -9.9) * mm});
            skLineSegment(sketch, "E78.left", {"start": v(-124.8, -36.2) * mm, "end": v(-124.8, -9.9) * mm});
            skLineSegment(sketch, "E78.right", {"start": v(-156.46, -36.2) * mm, "end": v(-156.46, -9.9) * mm});
            skLineSegment(sketch, "E79.bottom", {"start": v(-138.7, -95.23) * mm, "end": v(-133.05, -95.23) * mm});
            skLineSegment(sketch, "E79.top", {"start": v(-138.7, -78.22) * mm, "end": v(-133.05, -78.22) * mm});
            skLineSegment(sketch, "E79.left", {"start": v(-138.7, -95.23) * mm, "end": v(-138.7, -78.22) * mm});
            skLineSegment(sketch, "E79.right", {"start": v(-133.05, -95.23) * mm, "end": v(-133.05, -78.22) * mm});
            skSolve(sketch);
        }
        {
            var Q0;
            Q0 = qSketchRegion(id + "F15", true);
            extrude(context, id + "F16", {"entities" : qUnion([Q0]), "depth" : 50.8 * mm});
        }
    });
